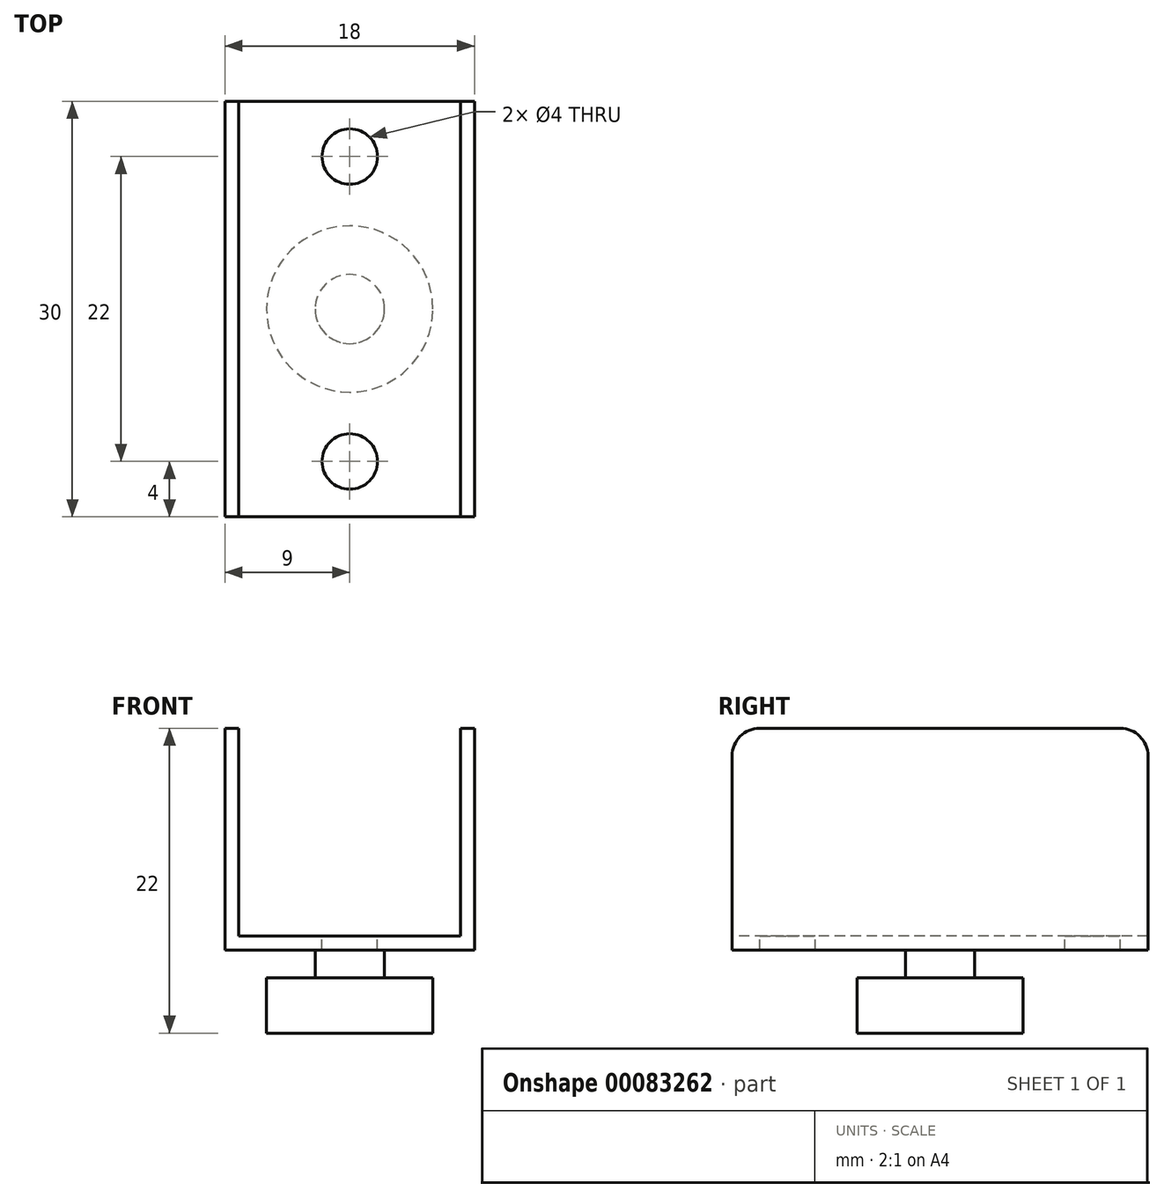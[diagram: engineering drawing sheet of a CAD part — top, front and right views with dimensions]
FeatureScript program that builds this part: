
annotation { "Feature Type Name" : "Feature", "Feature Type Description" : "" }
export const myFeature = defineFeature(function(context is Context, id is Id, definition is map)
    precondition{}
    {
        {
            var Q0;
            Q0=qCreatedBy(makeId("Front.planeOp"),FACE);
            var sketch = newSketch(context, id + "F0", { "sketchPlane" : qUnion([Q0])});
            skLineSegment(sketch, "E0.bottom", {"start": v(0, 0) * mm, "end": v(18, 0) * mm});
            skLineSegment(sketch, "E0.top", {"start": v(1, 1) * mm, "end": v(17, 1) * mm});
            skLineSegment(sketch, "E0.left", {"start": v(0, 0) * mm, "end": v(0, 1) * mm});
            skLineSegment(sketch, "E0.right", {"start": v(18, 0) * mm, "end": v(18, 1) * mm});
            skLineSegment(sketch, "E1.top", {"start": v(0, 16) * mm, "end": v(1, 16) * mm});
            skLineSegment(sketch, "E1.left", {"start": v(0, 1) * mm, "end": v(0, 16) * mm});
            skLineSegment(sketch, "E1.right", {"start": v(1, 1) * mm, "end": v(1, 16) * mm});
            skPoint(sketch, "E2.oppositeSnap0", {"position": v(0.5, 16) * mm});
            skLineSegment(sketch, "E2.top", {"start": v(18, 16) * mm, "end": v(17, 16) * mm});
            skLineSegment(sketch, "E2.left", {"start": v(18, 1) * mm, "end": v(18, 16) * mm});
            skLineSegment(sketch, "E2.right", {"start": v(17, 1) * mm, "end": v(17, 16) * mm});
            skSolve(sketch);
        }
        {
            var Q0;
            Q0=makeQuery(id+"F0.imprint","IMPRINT",FACE,{"disambiguationData":[TD([[makeQuery(id+"F0.imprint","IMPRINT",EDGE,{"derivedFrom":sQuery(id+"F0.wireOp",EDGE,"E0.bottom")}),1.0]])]});
            extrude(context, id + "F1", {"entities" : qUnion([Q0]), "oppositeDirection" : true, "depth" : 30 * mm});
        }
        {
            var Q0;
            Q0=makeQuery(id+"F1.opExtrude","SWEPT_FACE",FACE,{"disambiguationData":[OSD([sQuery(id+"F0.wireOp",EDGE,"E0.top")])]});
            var sketch = newSketch(context, id + "F2", { "sketchPlane" : qUnion([Q0])});
            skLineSegment(sketch, "E3.0", {"start": v(1, 30) * mm, "end": v(17, 30) * mm});
            skLineSegment(sketch, "E3.1", {"start": v(1, 30) * mm, "end": v(1, 0) * mm});
            skLineSegment(sketch, "E3.2", {"start": v(17, 30) * mm, "end": v(17, 0) * mm});
            skLineSegment(sketch, "E3.3", {"start": v(1, 0) * mm, "end": v(17, 0) * mm});
            skLineSegment(sketch, "E4", {"start": v(9, 30) * mm, "end": v(9, 0) * mm, "construction": true});
            skLineSegment(sketch, "E5", {"start": v(1, 15) * mm, "end": v(17, 15) * mm, "construction": true});
            skPoint(sketch, "E6", {"position": v(9, 15) * mm});
            skCircle(sketch, "E7", {"center": v(9, 15) * mm, "radius": 2.5 * mm});
            skPoint(sketch, "E8", {"position": v(9, 4) * mm});
            skPoint(sketch, "E9", {"position": v(9, 26) * mm});
            skSolve(sketch);
        }
        {
            var Q0;
            Q0=makeQuery(id+"F2.imprint","IMPRINT",FACE,{"disambiguationData":[TD([[makeQuery(id+"F2.imprint","IMPRINT",EDGE,{"derivedFrom":sQuery(id+"F2.wireOp",EDGE,"E7")}),1.0]])]});
            extrude(context, id + "F3", {"entities" : qUnion([Q0]), "operationType" : NewBodyOperationType.ADD, "oppositeDirection" : true, "depth" : 3 * mm});
        }
        {
            var Q0;
            Q0=makeQuery(id+"F3.opExtrude","CAP_FACE",FACE,{"disambiguationData":[OSD([sQuery(id+"F2.wireOp",EDGE,"E7")])],"isStart":false});
            var sketch = newSketch(context, id + "F4", { "sketchPlane" : qUnion([Q0])});
            skPoint(sketch, "E10", {"position": v(9, -15) * mm});
            skCircle(sketch, "E11", {"center": v(9, -15) * mm, "radius": 6 * mm});
            skSolve(sketch);
        }
        {
            var Q0;
            Q0=makeQuery(id+"F4.imprint","IMPRINT",FACE,{"disambiguationData":[TD([[makeQuery(id+"F4.imprint","IMPRINT",EDGE,{"derivedFrom":sQuery(id+"F4.wireOp",EDGE,"E11")}),1.0]])]});
            var Q1;
            Q1=makeQuery(id+"F4.imprint","IMPRINT",FACE,{"disambiguationData":[TD([[makeQuery(id+"F4.imprint","IMPRINT",EDGE,{"derivedFrom":makeQuery(id+"F3.opExtrude","CAP_EDGE",EDGE,{"disambiguationData":[OSD([sQuery(id+"F2.wireOp",EDGE,"E7")])],"isStart":false})}),-1.0]])]});
            extrude(context, id + "F5", {"entities" : qUnion([Q0, Q1]), "operationType" : NewBodyOperationType.ADD, "depth" : 4 * mm});
        }
        {
            var Q0;
            Q0=makeQuery(id+"F1.opExtrude","CAP_EDGE",EDGE,{"disambiguationData":[OSD([sQuery(id+"F0.wireOp",EDGE,"E2.top")])],"isStart":true});
            var Q1;
            Q1=makeQuery(id+"F1.opExtrude","CAP_EDGE",EDGE,{"disambiguationData":[OSD([sQuery(id+"F0.wireOp",EDGE,"E2.top")])],"isStart":false});
            var Q2;
            Q2=makeQuery(id+"F1.opExtrude","CAP_EDGE",EDGE,{"disambiguationData":[OSD([sQuery(id+"F0.wireOp",EDGE,"E1.top")])],"isStart":false});
            var Q3;
            Q3=makeQuery(id+"F1.opExtrude","CAP_EDGE",EDGE,{"disambiguationData":[OSD([sQuery(id+"F0.wireOp",EDGE,"E1.top")])],"isStart":true});
            fillet(context, id + "F6", {"entities" : qUnion([Q0, Q1, Q2, Q3]), "radius" : 2 * mm, "tangentPropagation" : true, "allowEdgeOverflow" : false});
        }
        {
            var Q0;
            Q0=sQuery(id+"F2.wireOp",VERTEX,"E8");
            var Q1;
            Q1=sQuery(id+"F2.wireOp",VERTEX,"E9");
            var Q2;
            Q2=makeQuery(id+"F1.opExtrude","SWEPT_BODY",BODY,{"disambiguationData":[OSD([sQuery(id+"F0.wireOp",EDGE,"E0.bottom"),sQuery(id+"F0.wireOp",EDGE,"E0.top"),sQuery(id+"F0.wireOp",EDGE,"E0.left"),sQuery(id+"F0.wireOp",EDGE,"E0.right"),sQuery(id+"F0.wireOp",EDGE,"E1.top"),sQuery(id+"F0.wireOp",EDGE,"E1.left"),sQuery(id+"F0.wireOp",EDGE,"E1.right"),sQuery(id+"F0.wireOp",EDGE,"E2.top"),sQuery(id+"F0.wireOp",EDGE,"E2.left"),sQuery(id+"F0.wireOp",EDGE,"E2.right")])]});
            hole(context, id + "F7", {"style" : HoleStyle.SIMPLE, "endStyle" : HoleEndStyle.BLIND, "holeDiameter" : 4 * mm, "holeDepth" : 15 * mm, "locations" : qUnion([Q0, Q1]), "scope" : qUnion([Q2])});
        }
    });
